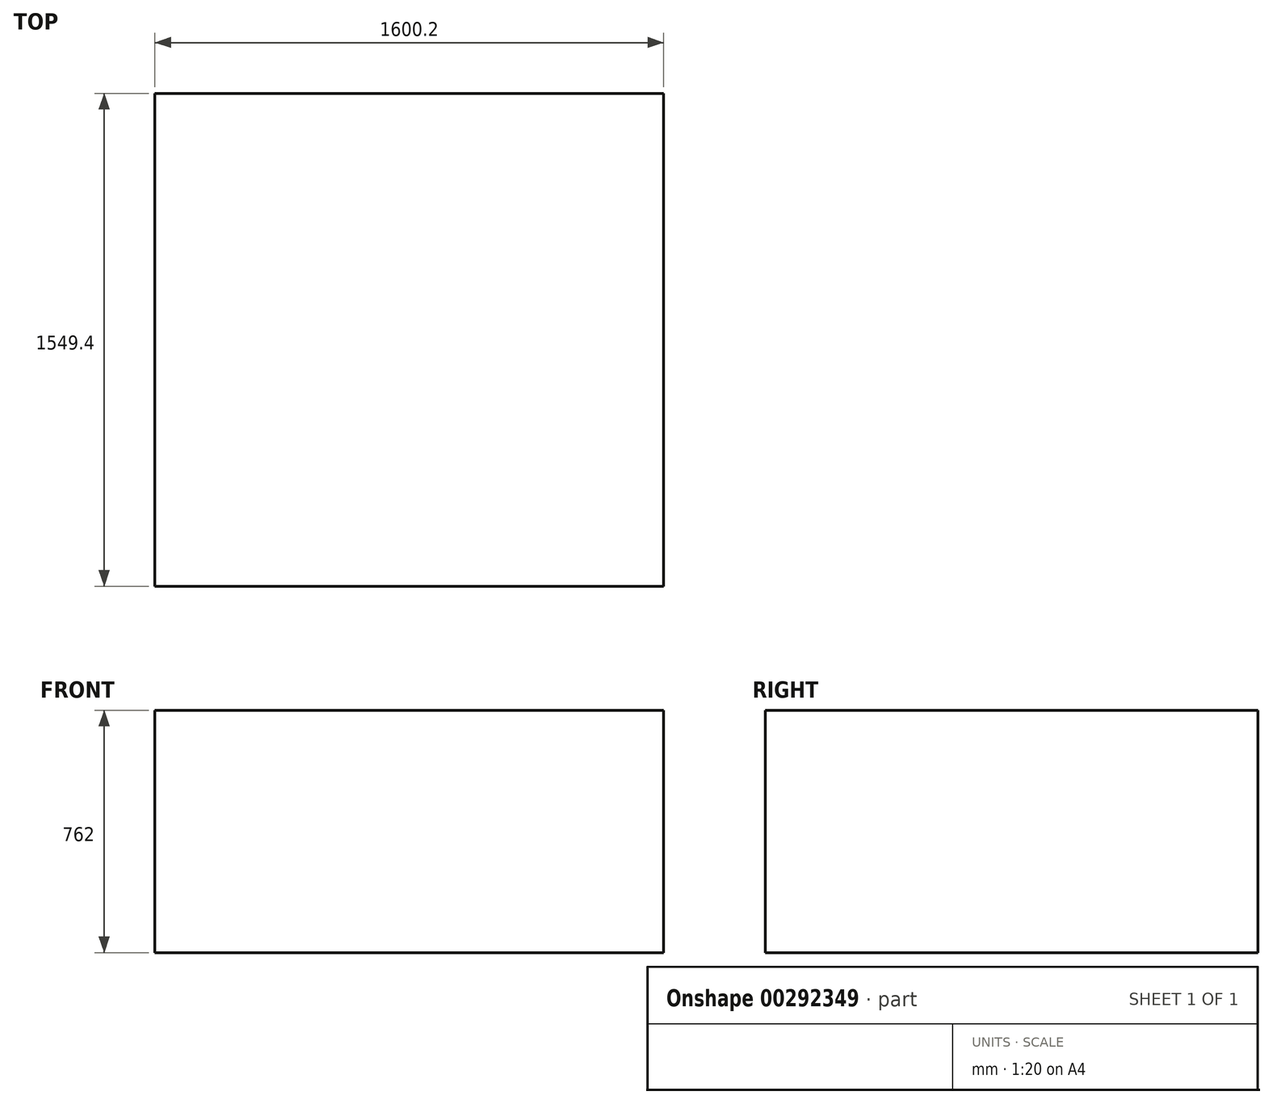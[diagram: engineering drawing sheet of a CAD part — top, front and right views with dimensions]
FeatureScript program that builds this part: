
annotation { "Feature Type Name" : "Feature", "Feature Type Description" : "" }
export const myFeature = defineFeature(function(context is Context, id is Id, definition is map)
    precondition{}
    {
        {
            var Q0;
            Q0=qCreatedBy(makeId("Top.planeOp"),FACE);
            var sketch = newSketch(context, id + "F0", { "sketchPlane" : qUnion([Q0])});
            skLineSegment(sketch, "E0.bottom", {"start": v(0, 774.7) * mm, "end": v(1600.2, 774.7) * mm});
            skLineSegment(sketch, "E0.top", {"start": v(0, -774.7) * mm, "end": v(1600.2, -774.7) * mm});
            skLineSegment(sketch, "E0.left", {"start": v(0, 774.7) * mm, "end": v(0, -774.7) * mm});
            skLineSegment(sketch, "E0.right", {"start": v(1600.2, 774.7) * mm, "end": v(1600.2, -774.7) * mm});
            skPoint(sketch, "E1.0", {"position": v(0, 0) * mm});
            skSolve(sketch);
        }
        {
            var Q0;
            Q0=qSketchRegion(id+"F0",true);
            extrude(context, id + "F1", {"entities" : qUnion([Q0]), "oppositeDirection" : true, "depth" : 762 * mm});
        }
    });
